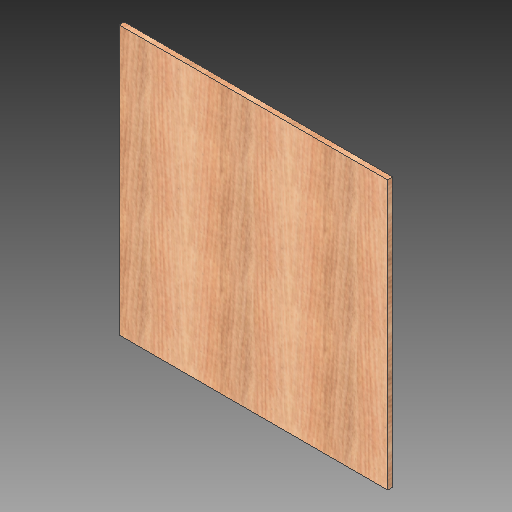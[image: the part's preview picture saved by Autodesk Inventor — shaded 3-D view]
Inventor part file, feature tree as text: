
AUTODESK INVENTOR PART (.ipt)
format: ipt  version: 2018 (Build 220112000, 112)  size: 277,504 bytes
history: native  units: in
note: dims shown in document units (in); Inventor stores cm internally (conversion verified against a paired STEP export)
features: extrude x1, sketch x1
ambient origin geometry x8: Origin, YZ Plane, XZ Plane, XY Plane, X Axis, Y Axis, Z Axis, Center Point
bodies: Solid1 (feature_tree)
feature tree (2):
  extrude  "Extrusion1"  Depth=26.0in
  sketch  "Sketch1"  dims[d0=26.0in d1=26.0in d2=0.5in d3=0.0in]
